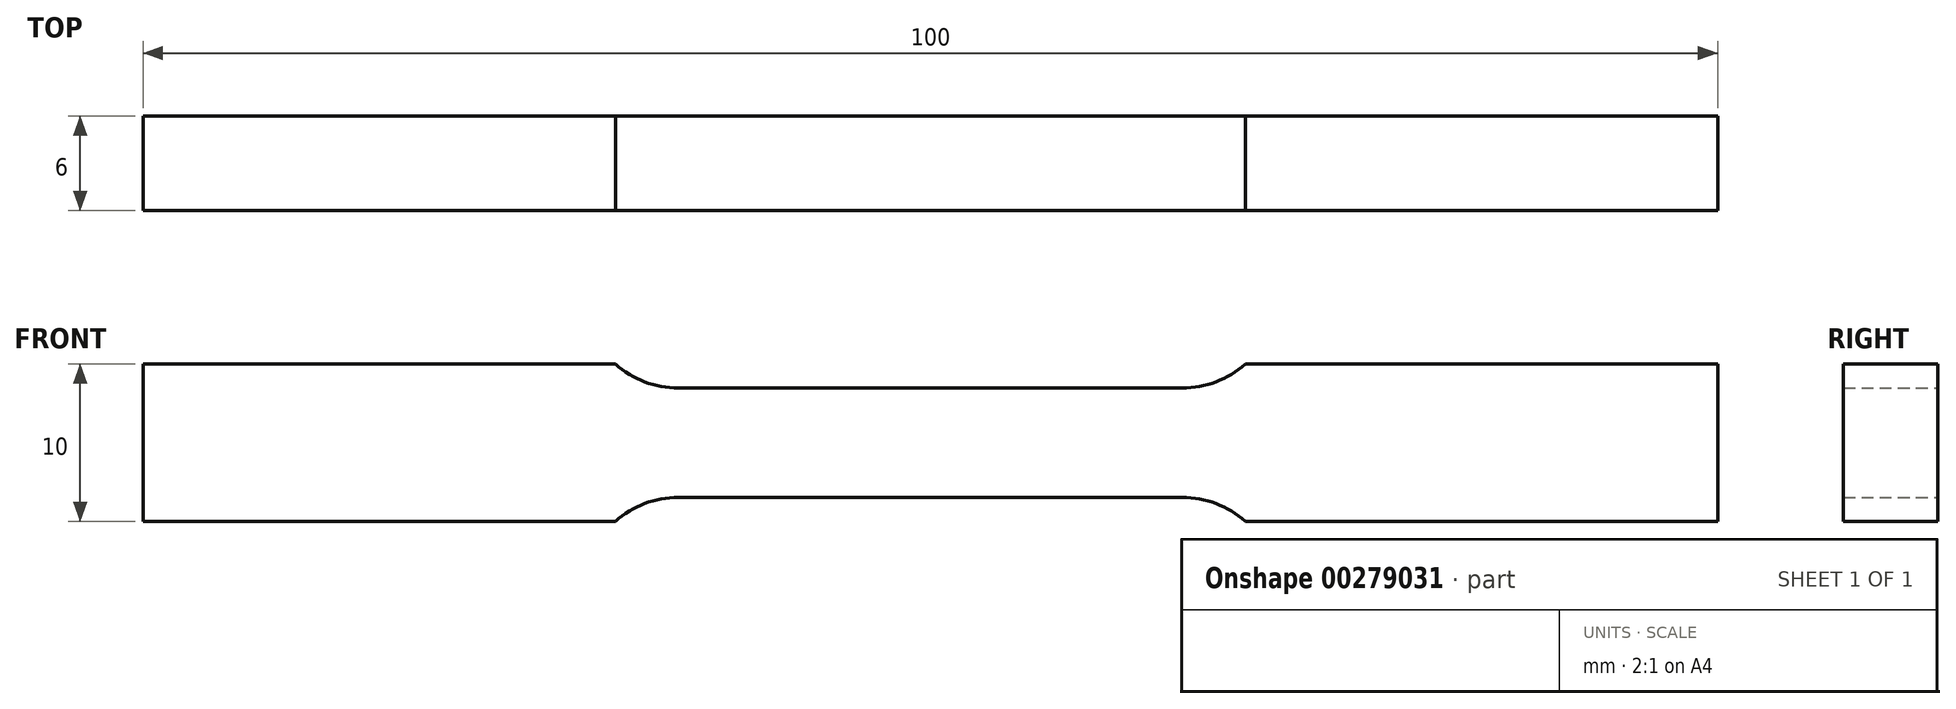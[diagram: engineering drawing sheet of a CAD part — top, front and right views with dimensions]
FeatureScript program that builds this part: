
annotation { "Feature Type Name" : "Feature", "Feature Type Description" : "" }
export const myFeature = defineFeature(function(context is Context, id is Id, definition is map)
    precondition{}
    {
        {
            var Q0;
            Q0=qCreatedBy(makeId("Front.planeOp"),FACE);
            var sketch = newSketch(context, id + "F0", { "sketchPlane" : qUnion([Q0])});
            skLineSegment(sketch, "E0", {"start": v(0, 3.47) * mm, "end": v(16, 3.47) * mm});
            skArc(sketch, "E1", {"start": v(16, 3.47) * mm, "mid": v(18.14, 3.87) * mm, "end": v(20, 5) * mm});
            skLineSegment(sketch, "E2", {"start": v(20, 5) * mm, "end": v(50, 5) * mm});
            skLineSegment(sketch, "E3", {"start": v(50, 5) * mm, "end": v(50, 0) * mm});
            skLineSegment(sketch, "E4.MirrorCS", {"start": v(0, -3.47) * mm, "end": v(16, -3.47) * mm});
            skLineSegment(sketch, "E5.MirrorCS", {"start": v(20, -5) * mm, "end": v(50, -5) * mm});
            skArc(sketch, "E6.MirrorCS", {"start": v(16, -3.47) * mm, "mid": v(18.14, -3.87) * mm, "end": v(20, -5) * mm});
            skLineSegment(sketch, "E7.MirrorCS", {"start": v(50, -5) * mm, "end": v(50, 0) * mm});
            skLineSegment(sketch, "E8.MirrorCS", {"start": v(-50, -5) * mm, "end": v(-50, 0) * mm});
            skArc(sketch, "E9.MirrorCS", {"start": v(-16, -3.47) * mm, "mid": v(-18.14, -3.87) * mm, "end": v(-20, -5) * mm});
            skArc(sketch, "E10.MirrorCS", {"start": v(-16, 3.47) * mm, "mid": v(-18.14, 3.87) * mm, "end": v(-20, 5) * mm});
            skLineSegment(sketch, "E11.MirrorCS", {"start": v(-20, 5) * mm, "end": v(-50, 5) * mm});
            skLineSegment(sketch, "E12.MirrorCS", {"start": v(-20, -5) * mm, "end": v(-50, -5) * mm});
            skLineSegment(sketch, "E13.MirrorCS", {"start": v(0, -3.47) * mm, "end": v(-16, -3.47) * mm});
            skLineSegment(sketch, "E14.MirrorCS", {"start": v(-50, 5) * mm, "end": v(-50, 0) * mm});
            skLineSegment(sketch, "E15.MirrorCS", {"start": v(0, 3.47) * mm, "end": v(-16, 3.47) * mm});
            skSolve(sketch);
        }
        {
            var Q0;
            Q0=makeQuery(id+"F0.imprint","IMPRINT",FACE,{"disambiguationData":[TD([[makeQuery(id+"F0.imprint","IMPRINT",EDGE,{"derivedFrom":sQuery(id+"F0.wireOp",EDGE,"E0")}),-1.0]])]});
            extrude(context, id + "F1", {"entities" : qUnion([Q0]), "endBound" : BoundingType.SYMMETRIC, "depth" : 6 * mm});
        }
    });
